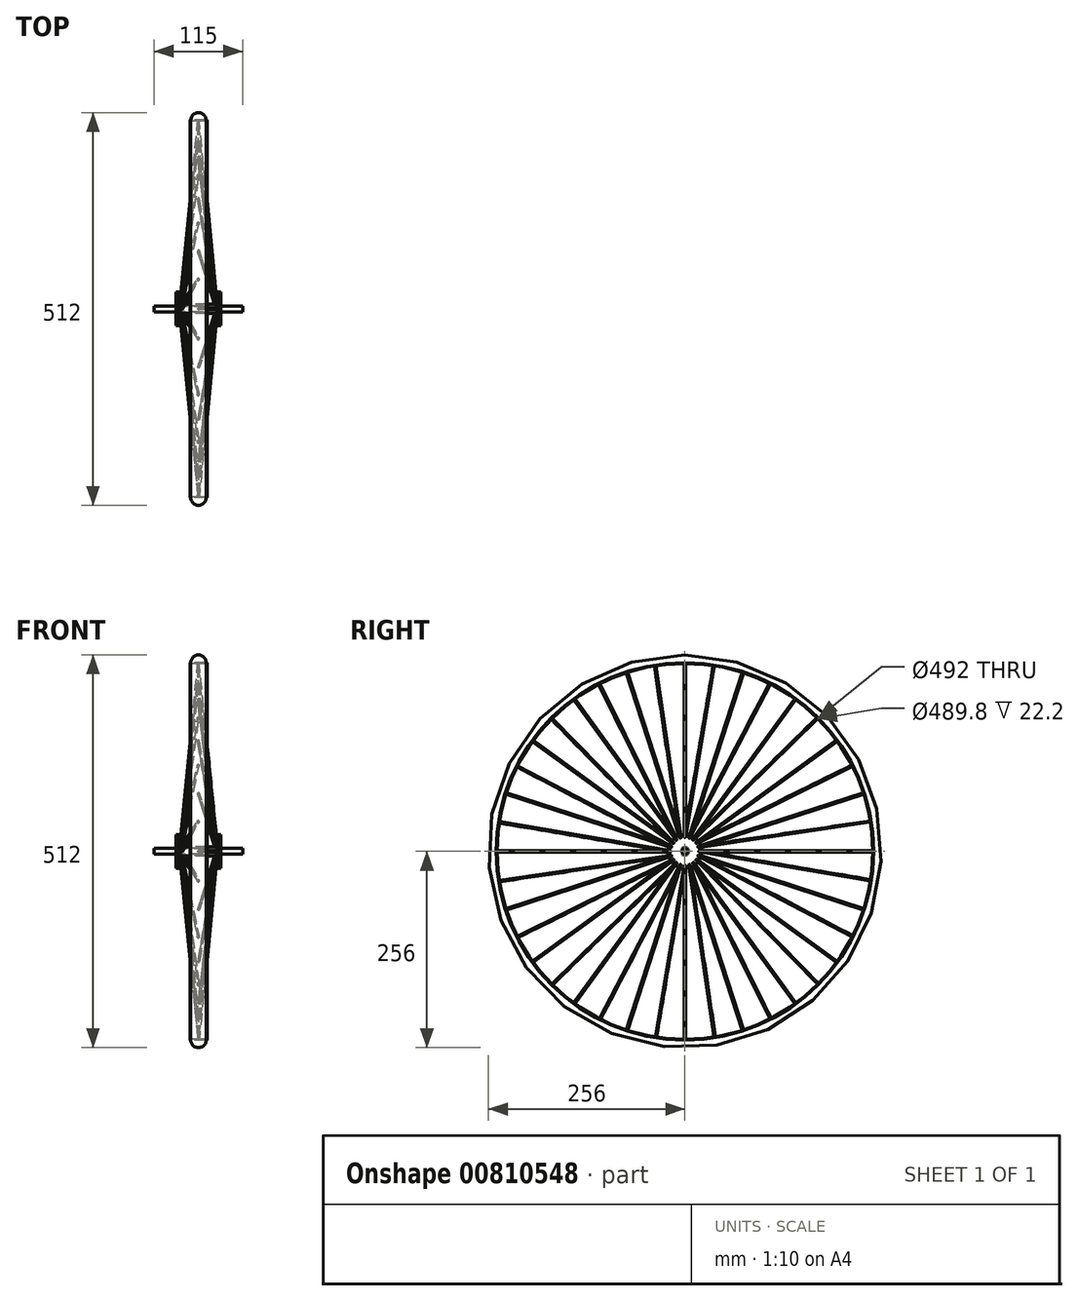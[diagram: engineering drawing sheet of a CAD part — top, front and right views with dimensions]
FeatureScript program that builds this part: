
annotation { "Feature Type Name" : "Feature", "Feature Type Description" : "" }
export const myFeature = defineFeature(function(context is Context, id is Id, definition is map)
    precondition{}
    {
        {
            var Q0;
            Q0=qCreatedBy(makeId("Right.planeOp"),FACE);
            var sketch = newSketch(context, id + "F0", { "sketchPlane" : qUnion([Q0])});
            skCircle(sketch, "E0", {"center": v(0, 0) * mm, "radius": 4 * mm});
            skSolve(sketch);
        }
        {
            var Q0;
            Q0=qCreatedBy(makeId("Front.planeOp"),FACE);
            var sketch = newSketch(context, id + "F1", { "sketchPlane" : qUnion([Q0])});
            skLineSegment(sketch, "E1", {"start": v(0, 6) * mm, "end": v(25, 6) * mm});
            skLineSegment(sketch, "E2", {"start": v(25, 6) * mm, "end": v(25, 22) * mm});
            skLineSegment(sketch, "E3", {"start": v(25, 22) * mm, "end": v(29, 22) * mm});
            skLineSegment(sketch, "E4", {"start": v(29, 22) * mm, "end": v(29, 0) * mm});
            skLineSegment(sketch, "E5", {"start": v(-60.28, 0) * mm, "end": v(66.23, 0) * mm, "construction": true});
            skLineSegment(sketch, "E6.MirrorCS", {"start": v(-29, 22) * mm, "end": v(-29, 0) * mm});
            skLineSegment(sketch, "E7.MirrorCS", {"start": v(-25, 22) * mm, "end": v(-29, 22) * mm});
            skLineSegment(sketch, "E8.MirrorCS", {"start": v(0, 6) * mm, "end": v(-25, 6) * mm});
            skLineSegment(sketch, "E9.MirrorCS", {"start": v(-25, 6) * mm, "end": v(-25, 22) * mm});
            skLineSegment(sketch, "E10", {"start": v(-29, 0) * mm, "end": v(29, 0) * mm});
            skSolve(sketch);
        }
        {
            var Q0;
            Q0 = qSketchRegion(id + "F1", true);
            var Q1;
            Q1=sQuery(id+"F1.wireOp",EDGE,"E5");
            revolve(context, id + "F2", {"surfaceOperationType" : NewSurfaceOperationType.NEW, "entities" : qUnion([Q0]), "axis" : qUnion([Q1]), "revolveType" : RevolveType.FULL});
        }
        {
            var Q0;
            Q0=makeQuery(id+"F2.opRevolve","SWEPT_FACE",FACE,{"disambiguationData":[OSD([sQuery(id+"F1.wireOp",EDGE,"E4")])]});
            var sketch = newSketch(context, id + "F3", { "sketchPlane" : qUnion([Q0])});
            skCircle(sketch, "E11", {"center": v(0, 19) * mm, "radius": 1 * mm});
            skCircle(sketch, "E12.1.0", {"center": v(-5.87, 18.07) * mm, "radius": 1 * mm});
            skCircle(sketch, "E12.2.0", {"center": v(-11.17, 15.37) * mm, "radius": 1 * mm});
            skPoint(sketch, "E12.center", {"position": v(0, 0) * mm});
            skCircle(sketch, "E13.1.3.0", {"center": v(-15.37, 11.17) * mm, "radius": 1 * mm});
            skCircle(sketch, "E13.1.4.0", {"center": v(-18.07, 5.87) * mm, "radius": 1 * mm});
            skCircle(sketch, "E13.1.5.0", {"center": v(-19, 0) * mm, "radius": 1 * mm});
            skCircle(sketch, "E13.1.6.0", {"center": v(-18.07, -5.87) * mm, "radius": 1 * mm});
            skCircle(sketch, "E13.1.7.0", {"center": v(-15.37, -11.17) * mm, "radius": 1 * mm});
            skCircle(sketch, "E13.1.8.0", {"center": v(-11.17, -15.37) * mm, "radius": 1 * mm});
            skCircle(sketch, "E13.1.9.0", {"center": v(-5.87, -18.07) * mm, "radius": 1 * mm});
            skCircle(sketch, "E13.1.10.0", {"center": v(0, -19) * mm, "radius": 1 * mm});
            skCircle(sketch, "E13.1.11.0", {"center": v(5.87, -18.07) * mm, "radius": 1 * mm});
            skCircle(sketch, "E13.1.12.0", {"center": v(11.17, -15.37) * mm, "radius": 1 * mm});
            skCircle(sketch, "E13.1.13.0", {"center": v(15.37, -11.17) * mm, "radius": 1 * mm});
            skCircle(sketch, "E13.1.14.0", {"center": v(18.07, -5.87) * mm, "radius": 1 * mm});
            skCircle(sketch, "E13.1.15.0", {"center": v(19, 0) * mm, "radius": 1 * mm});
            skCircle(sketch, "E13.1.16.0", {"center": v(18.07, 5.87) * mm, "radius": 1 * mm});
            skCircle(sketch, "E13.1.17.0", {"center": v(15.37, 11.17) * mm, "radius": 1 * mm});
            skCircle(sketch, "E13.1.18.0", {"center": v(11.17, 15.37) * mm, "radius": 1 * mm});
            skCircle(sketch, "E13.1.19.0", {"center": v(5.87, 18.07) * mm, "radius": 1 * mm});
            skSolve(sketch);
        }
        {
            var Q0;
            Q0=makeQuery(id+"F3.imprint","IMPRINT",FACE,{"disambiguationData":[TD([[makeQuery(id+"F3.imprint","IMPRINT",EDGE,{"derivedFrom":sQuery(id+"F3.wireOp",EDGE,"E13.1.25.0")}),1.0]])]});
            var Q1;
            Q1=makeQuery(id+"F3.imprint","IMPRINT",FACE,{"disambiguationData":[TD([[makeQuery(id+"F3.imprint","IMPRINT",EDGE,{"derivedFrom":sQuery(id+"F3.wireOp",EDGE,"E13.1.27.0")}),1.0]])]});
            var Q2;
            Q2=makeQuery(id+"F3.imprint","IMPRINT",FACE,{"disambiguationData":[TD([[makeQuery(id+"F3.imprint","IMPRINT",EDGE,{"derivedFrom":sQuery(id+"F3.wireOp",EDGE,"E11")}),1.0]])]});
            var Q3;
            Q3=makeQuery(id+"F3.imprint","IMPRINT",FACE,{"disambiguationData":[TD([[makeQuery(id+"F3.imprint","IMPRINT",EDGE,{"derivedFrom":sQuery(id+"F3.wireOp",EDGE,"E12.1.0")}),1.0]])]});
            var Q4;
            Q4=makeQuery(id+"F3.imprint","IMPRINT",FACE,{"disambiguationData":[TD([[makeQuery(id+"F3.imprint","IMPRINT",EDGE,{"derivedFrom":sQuery(id+"F3.wireOp",EDGE,"E12.2.0")}),1.0]])]});
            var Q5;
            Q5=makeQuery(id+"F3.imprint","IMPRINT",FACE,{"disambiguationData":[TD([[makeQuery(id+"F3.imprint","IMPRINT",EDGE,{"derivedFrom":sQuery(id+"F3.wireOp",EDGE,"E13.1.3.0")}),1.0]])]});
            var Q6;
            Q6=makeQuery(id+"F3.imprint","IMPRINT",FACE,{"disambiguationData":[TD([[makeQuery(id+"F3.imprint","IMPRINT",EDGE,{"derivedFrom":sQuery(id+"F3.wireOp",EDGE,"E13.1.4.0")}),1.0]])]});
            var Q7;
            Q7=makeQuery(id+"F3.imprint","IMPRINT",FACE,{"disambiguationData":[TD([[makeQuery(id+"F3.imprint","IMPRINT",EDGE,{"derivedFrom":sQuery(id+"F3.wireOp",EDGE,"E13.1.5.0")}),1.0]])]});
            var Q8;
            Q8=makeQuery(id+"F3.imprint","IMPRINT",FACE,{"disambiguationData":[TD([[makeQuery(id+"F3.imprint","IMPRINT",EDGE,{"derivedFrom":sQuery(id+"F3.wireOp",EDGE,"E13.1.6.0")}),1.0]])]});
            var Q9;
            Q9=makeQuery(id+"F3.imprint","IMPRINT",FACE,{"disambiguationData":[TD([[makeQuery(id+"F3.imprint","IMPRINT",EDGE,{"derivedFrom":sQuery(id+"F3.wireOp",EDGE,"E13.1.7.0")}),1.0]])]});
            var Q10;
            Q10=makeQuery(id+"F3.imprint","IMPRINT",FACE,{"disambiguationData":[TD([[makeQuery(id+"F3.imprint","IMPRINT",EDGE,{"derivedFrom":sQuery(id+"F3.wireOp",EDGE,"E13.1.8.0")}),1.0]])]});
            var Q11;
            Q11=makeQuery(id+"F3.imprint","IMPRINT",FACE,{"disambiguationData":[TD([[makeQuery(id+"F3.imprint","IMPRINT",EDGE,{"derivedFrom":sQuery(id+"F3.wireOp",EDGE,"E13.1.9.0")}),1.0]])]});
            var Q12;
            Q12=makeQuery(id+"F3.imprint","IMPRINT",FACE,{"disambiguationData":[TD([[makeQuery(id+"F3.imprint","IMPRINT",EDGE,{"derivedFrom":sQuery(id+"F3.wireOp",EDGE,"E13.1.10.0")}),1.0]])]});
            var Q13;
            Q13=makeQuery(id+"F3.imprint","IMPRINT",FACE,{"disambiguationData":[TD([[makeQuery(id+"F3.imprint","IMPRINT",EDGE,{"derivedFrom":sQuery(id+"F3.wireOp",EDGE,"E13.1.11.0")}),1.0]])]});
            var Q14;
            Q14=makeQuery(id+"F3.imprint","IMPRINT",FACE,{"disambiguationData":[TD([[makeQuery(id+"F3.imprint","IMPRINT",EDGE,{"derivedFrom":sQuery(id+"F3.wireOp",EDGE,"E13.1.12.0")}),1.0]])]});
            var Q15;
            Q15=makeQuery(id+"F3.imprint","IMPRINT",FACE,{"disambiguationData":[TD([[makeQuery(id+"F3.imprint","IMPRINT",EDGE,{"derivedFrom":sQuery(id+"F3.wireOp",EDGE,"E13.1.13.0")}),1.0]])]});
            var Q16;
            Q16=makeQuery(id+"F3.imprint","IMPRINT",FACE,{"disambiguationData":[TD([[makeQuery(id+"F3.imprint","IMPRINT",EDGE,{"derivedFrom":sQuery(id+"F3.wireOp",EDGE,"E13.1.14.0")}),1.0]])]});
            var Q17;
            Q17=makeQuery(id+"F3.imprint","IMPRINT",FACE,{"disambiguationData":[TD([[makeQuery(id+"F3.imprint","IMPRINT",EDGE,{"derivedFrom":sQuery(id+"F3.wireOp",EDGE,"E13.1.15.0")}),1.0]])]});
            var Q18;
            Q18=makeQuery(id+"F3.imprint","IMPRINT",FACE,{"disambiguationData":[TD([[makeQuery(id+"F3.imprint","IMPRINT",EDGE,{"derivedFrom":sQuery(id+"F3.wireOp",EDGE,"E13.1.18.0")}),1.0]])]});
            var Q19;
            Q19=makeQuery(id+"F3.imprint","IMPRINT",FACE,{"disambiguationData":[TD([[makeQuery(id+"F3.imprint","IMPRINT",EDGE,{"derivedFrom":sQuery(id+"F3.wireOp",EDGE,"E13.1.17.0")}),1.0]])]});
            var Q20;
            Q20=makeQuery(id+"F3.imprint","IMPRINT",FACE,{"disambiguationData":[TD([[makeQuery(id+"F3.imprint","IMPRINT",EDGE,{"derivedFrom":sQuery(id+"F3.wireOp",EDGE,"E13.1.16.0")}),1.0]])]});
            var Q21;
            Q21=makeQuery(id+"F3.imprint","IMPRINT",FACE,{"disambiguationData":[TD([[makeQuery(id+"F3.imprint","IMPRINT",EDGE,{"derivedFrom":sQuery(id+"F3.wireOp",EDGE,"E13.1.19.0")}),1.0]])]});
            var Q22;
            Q22=makeQuery(id+"F3.imprint","IMPRINT",FACE,{"disambiguationData":[TD([[makeQuery(id+"F3.imprint","IMPRINT",EDGE,{"derivedFrom":sQuery(id+"F3.wireOp",EDGE,"E13.1.20.0")}),1.0]])]});
            var Q23;
            Q23=makeQuery(id+"F3.imprint","IMPRINT",FACE,{"disambiguationData":[TD([[makeQuery(id+"F3.imprint","IMPRINT",EDGE,{"derivedFrom":sQuery(id+"F3.wireOp",EDGE,"E13.1.21.0")}),1.0]])]});
            var Q24;
            Q24=makeQuery(id+"F3.imprint","IMPRINT",FACE,{"disambiguationData":[TD([[makeQuery(id+"F3.imprint","IMPRINT",EDGE,{"derivedFrom":sQuery(id+"F3.wireOp",EDGE,"E13.1.22.0")}),1.0]])]});
            var Q25;
            Q25=makeQuery(id+"F3.imprint","IMPRINT",FACE,{"disambiguationData":[TD([[makeQuery(id+"F3.imprint","IMPRINT",EDGE,{"derivedFrom":sQuery(id+"F3.wireOp",EDGE,"E13.1.24.0")}),1.0]])]});
            var Q26;
            Q26=makeQuery(id+"F3.imprint","IMPRINT",FACE,{"disambiguationData":[TD([[makeQuery(id+"F3.imprint","IMPRINT",EDGE,{"derivedFrom":sQuery(id+"F3.wireOp",EDGE,"E13.1.26.0")}),1.0]])]});
            var Q27;
            Q27=makeQuery(id+"F3.imprint","IMPRINT",FACE,{"disambiguationData":[TD([[makeQuery(id+"F3.imprint","IMPRINT",EDGE,{"derivedFrom":sQuery(id+"F3.wireOp",EDGE,"E13.1.23.0")}),1.0]])]});
            extrude(context, id + "F4", {"entities" : qUnion([Q0, Q1, Q2, Q3, Q4, Q5, Q6, Q7, Q8, Q9, Q10, Q11, Q12, Q13, Q14, Q15, Q16, Q17, Q18, Q19, Q20, Q21, Q22, Q23, Q24, Q25, Q26, Q27]), "operationType" : NewBodyOperationType.REMOVE, "endBound" : BoundingType.THROUGH_ALL, "oppositeDirection" : true, "depth" : 25 * mm, "offsetDistance" : 25 * mm});
        }
        {
            var Q0;
            Q0=qCreatedBy(makeId("Front.planeOp"),FACE);
            var sketch = newSketch(context, id + "F5", { "sketchPlane" : qUnion([Q0])});
            skLineSegment(sketch, "E14", {"start": v(0, 0) * mm, "end": v(0, 256) * mm, "construction": true});
            skArc(sketch, "E15", {"start": v(10, 246) * mm, "mid": v(0, 256) * mm, "end": v(-10, 246) * mm});
            skLineSegment(sketch, "E16", {"start": v(-10, 246) * mm, "end": v(10, 246) * mm});
            skSolve(sketch);
        }
        {
            var Q0;
            Q0 = qSketchRegion(id + "F5", true);
            var Q1;
            Q1=sQuery(id+"F1.wireOp",EDGE,"E5");
            revolve(context, id + "F6", {"surfaceOperationType" : NewSurfaceOperationType.NEW, "entities" : qUnion([Q0]), "axis" : qUnion([Q1]), "revolveType" : RevolveType.FULL});
        }
        {
            var Q0;
            Q0=qCreatedBy(makeId("Front.planeOp"),FACE);
            var sketch = newSketch(context, id + "F7", { "sketchPlane" : qUnion([Q0])});
            skLineSegment(sketch, "E17", {"start": v(10.1, 245.9) * mm, "end": v(0, 245.9) * mm});
            skLineSegment(sketch, "E18", {"start": v(10.1, 245.9) * mm, "end": v(10.1, 246.1) * mm});
            skLineSegment(sketch, "E19.0", {"start": v(11.1, 244.9) * mm, "end": v(11.1, 246.1) * mm});
            skLineSegment(sketch, "E20.0", {"start": v(11.1, 244.9) * mm, "end": v(0, 244.9) * mm});
            skLineSegment(sketch, "E21.0", {"start": v(10.1, 244.9) * mm, "end": v(0, 244.9) * mm});
            skLineSegment(sketch, "E22", {"start": v(10.1, 246.1) * mm, "end": v(11.1, 246.1) * mm});
            skLineSegment(sketch, "E23.MirrorCS", {"start": v(-10.1, 245.9) * mm, "end": v(0, 245.9) * mm});
            skLineSegment(sketch, "E24.MirrorCS", {"start": v(-10.1, 246.1) * mm, "end": v(-11.1, 246.1) * mm});
            skLineSegment(sketch, "E25.MirrorCS", {"start": v(-11.1, 244.9) * mm, "end": v(0, 244.9) * mm});
            skLineSegment(sketch, "E26.MirrorCS", {"start": v(-11.1, 244.9) * mm, "end": v(-11.1, 246.1) * mm});
            skLineSegment(sketch, "E27.MirrorCS", {"start": v(-10.1, 245.9) * mm, "end": v(-10.1, 246.1) * mm});
            skSolve(sketch);
        }
        {
            var Q0;
            Q0=makeQuery(id+"F7.imprint","IMPRINT",FACE,{"disambiguationData":[TD([[makeQuery(id+"F7.imprint","IMPRINT",EDGE,{"derivedFrom":sQuery(id+"F7.wireOp",EDGE,"E17")}),1.0]])]});
            var Q1;
            Q1=sQuery(id+"F1.wireOp",EDGE,"E5");
            revolve(context, id + "F8", {"surfaceOperationType" : NewSurfaceOperationType.NEW, "entities" : qUnion([Q0]), "axis" : qUnion([Q1]), "revolveType" : RevolveType.FULL});
        }
        {
            var Q0;
            Q0=qCreatedBy(makeId("Top.planeOp"),FACE);
            var Q1;
            Q1=sQuery(id+"F7.wireOp",EDGE,"E21.0");
            cPlane(context, id + "F9", {"entities" : qUnion([Q0, Q1]), "cplaneType" : CPlaneType.LINE_ANGLE, "offset" : 25 * mm, "angle" : 180 * degree, "width" : 150 * mm, "height" : 150 * mm});
        }
        {
            var Q0;
            Q0=qCreatedBy(id+"F9.planeOp",FACE);
            var sketch = newSketch(context, id + "F10", { "sketchPlane" : qUnion([Q0])});
            skPoint(sketch, "E28", {"position": v(0, 0) * mm});
            skCircle(sketch, "E29", {"center": v(0, 0) * mm, "radius": 2.62 * mm});
            skSolve(sketch);
        }
        {
            var Q0;
            Q0=qCreatedBy(makeId("Front.planeOp"),FACE);
            var sketch = newSketch(context, id + "F11", { "sketchPlane" : qUnion([Q0])});
            skLineSegment(sketch, "E30", {"start": v(0, 244.9) * mm, "end": v(22.01, 21.7) * mm});
            skLineSegment(sketch, "E31", {"start": v(25, 19) * mm, "end": v(29, 19) * mm});
            skPoint(sketch, "E32.visualSharp", {"position": v(22.28, 19) * mm});
            skArc(sketch, "E32.filletArc", {"start": v(22.01, 21.7) * mm, "mid": v(22.99, 19.78) * mm, "end": v(25, 19) * mm});
            skSolve(sketch);
        }
        {
            var Q0;
            Q0=sQuery(id+"F10.wireOp",VERTEX,"E28");
            var Q1;
            Q1=qCreatedBy(makeId("Right.planeOp"),FACE);
            cPlane(context, id + "F12", {"entities" : qUnion([Q0, Q1]), "cplaneType" : CPlaneType.PLANE_POINT, "offset" : 25 * mm, "width" : 150 * mm, "height" : 150 * mm});
        }
        {
            var Q0;
            Q0=qCreatedBy(id+"F12.planeOp",FACE);
            var sketch = newSketch(context, id + "F13", { "sketchPlane" : qUnion([Q0])});
            skPoint(sketch, "E33.0", {"position": v(0, 244.9) * mm});
            skPoint(sketch, "E34.1.0", {"position": v(-38.31, 241.9) * mm});
            skPoint(sketch, "E34.2.0", {"position": v(-75.68, 232.92) * mm});
            skPoint(sketch, "E34.3.0", {"position": v(-111.19, 218.21) * mm});
            skPoint(sketch, "E34.4.0", {"position": v(-143.95, 198.13) * mm});
            skPoint(sketch, "E34.5.0", {"position": v(-173.18, 173.18) * mm});
            skPoint(sketch, "E34.6.0", {"position": v(-198.13, 143.95) * mm});
            skPoint(sketch, "E34.7.0", {"position": v(-218.21, 111.19) * mm});
            skPoint(sketch, "E34.8.0", {"position": v(-232.92, 75.68) * mm});
            skPoint(sketch, "E34.9.0", {"position": v(-241.9, 38.31) * mm});
            skPoint(sketch, "E34.10.0", {"position": v(-244.9, 0) * mm});
            skPoint(sketch, "E34.11.0", {"position": v(-241.9, -38.31) * mm});
            skPoint(sketch, "E34.12.0", {"position": v(-232.92, -75.68) * mm});
            skPoint(sketch, "E34.13.0", {"position": v(-218.21, -111.19) * mm});
            skPoint(sketch, "E34.14.0", {"position": v(-198.13, -143.95) * mm});
            skPoint(sketch, "E34.15.0", {"position": v(-173.18, -173.18) * mm});
            skPoint(sketch, "E34.16.0", {"position": v(-143.95, -198.13) * mm});
            skPoint(sketch, "E34.17.0", {"position": v(-111.19, -218.21) * mm});
            skPoint(sketch, "E34.18.0", {"position": v(-75.68, -232.92) * mm});
            skPoint(sketch, "E34.19.0", {"position": v(-38.31, -241.9) * mm});
            skPoint(sketch, "E34.20.0", {"position": v(0, -244.9) * mm});
            skPoint(sketch, "E34.21.0", {"position": v(38.31, -241.9) * mm});
            skPoint(sketch, "E34.22.0", {"position": v(75.68, -232.92) * mm});
            skPoint(sketch, "E34.23.0", {"position": v(111.19, -218.21) * mm});
            skPoint(sketch, "E34.24.0", {"position": v(143.95, -198.13) * mm});
            skPoint(sketch, "E34.25.0", {"position": v(173.18, -173.18) * mm});
            skPoint(sketch, "E34.26.0", {"position": v(198.13, -143.95) * mm});
            skPoint(sketch, "E34.27.0", {"position": v(218.21, -111.19) * mm});
            skPoint(sketch, "E34.28.0", {"position": v(232.92, -75.68) * mm});
            skPoint(sketch, "E34.29.0", {"position": v(241.9, -38.31) * mm});
            skPoint(sketch, "E34.30.0", {"position": v(244.9, 0) * mm});
            skPoint(sketch, "E34.31.0", {"position": v(241.9, 38.31) * mm});
            skPoint(sketch, "E34.32.0", {"position": v(232.92, 75.68) * mm});
            skPoint(sketch, "E34.33.0", {"position": v(218.21, 111.19) * mm});
            skPoint(sketch, "E34.34.0", {"position": v(198.13, 143.95) * mm});
            skPoint(sketch, "E34.35.0", {"position": v(173.18, 173.18) * mm});
            skPoint(sketch, "E34.36.0", {"position": v(143.95, 198.13) * mm});
            skPoint(sketch, "E34.37.0", {"position": v(111.19, 218.21) * mm});
            skPoint(sketch, "E34.38.0", {"position": v(75.68, 232.92) * mm});
            skPoint(sketch, "E34.39.0", {"position": v(38.31, 241.9) * mm});
            skPoint(sketch, "E34.center", {"position": v(0, 0) * mm});
            skSolve(sketch);
        }
        {
            var Q0;
            Q0=sQuery(id+"F13.wireOp",VERTEX,"E34.1.0");
            var Q1;
            Q1=sQuery(id+"F1.wireOp",VERTEX,"E5.end");
            var Q2;
            Q2=sQuery(id+"F1.wireOp",VERTEX,"E5.start");
            cPlane(context, id + "F14", {"entities" : qUnion([Q0, Q1, Q2]), "cplaneType" : CPlaneType.THREE_POINT, "offset" : 25 * mm, "width" : 150 * mm, "height" : 150 * mm});
        }
        {
            var Q0;
            Q0=sQuery(id+"F3.wireOp",VERTEX,"E11.center");
            var Q1;
            Q1=sQuery(id+"F11.wireOp",EDGE,"E31");
            cPlane(context, id + "F15", {"entities" : qUnion([Q0, Q1]), "cplaneType" : CPlaneType.LINE_POINT, "offset" : 25 * mm, "width" : 150 * mm, "height" : 150 * mm});
        }
        {
            var Q0;
            Q0=qCreatedBy(id+"F15.planeOp",FACE);
            var sketch = newSketch(context, id + "F16", { "sketchPlane" : qUnion([Q0])});
            skCircle(sketch, "E35", {"center": v(0, 19) * mm, "radius": 0.99 * mm});
            skSolve(sketch);
        }
        {
            var Q0;
            Q0 = qSketchRegion(id + "F16", true);
            var Q1;
            Q1=sQuery(id+"F11.wireOp",EDGE,"E31");
            var Q2;
            Q2=sQuery(id+"F11.wireOp",EDGE,"E32.filletArc");
            var Q3;
            Q3=sQuery(id+"F11.wireOp",EDGE,"E30");
            sweep(context, id + "F17", {"profiles" : qUnion([Q0]), "path" : qUnion([Q1, Q2, Q3])});
        }
        {
            var Q0;
            Q0=makeQuery(id+"F17.opSweep","SWEPT_BODY",BODY,{"disambiguationData":[OSD([sQuery(id+"F11.wireOp",EDGE,"E30"),sQuery(id+"F16.wireOp",EDGE,"E35")])]});
            var Q1;
            Q1=sQuery(id+"F1.wireOp",EDGE,"E5");
            circularPattern(context, id + "F18", {"operationType" : NewBodyOperationType.ADD, "entities" : qUnion([Q0]), "axis" : qUnion([Q1]), "angle" : 360 * degree, "instanceCount" : 20, "equalSpace" : true});
        }
        {
            var Q0;
            Q0=sQuery(id+"F1.wireOp",VERTEX,"E5.start");
            var Q1;
            Q1=sQuery(id+"F1.wireOp",EDGE,"E5");
            cPlane(context, id + "F19", {"entities" : qUnion([Q0, Q1]), "cplaneType" : CPlaneType.LINE_POINT, "offset" : 25 * mm, "width" : 150 * mm, "height" : 150 * mm});
        }
        {
            var Q0;
            Q0=qCreatedBy(id+"F19.planeOp",FACE);
            var sketch = newSketch(context, id + "F20", { "sketchPlane" : qUnion([Q0])});
            skLineSegment(sketch, "E36", {"start": v(0, 0) * mm, "end": v(0, 277.89) * mm, "construction": true});
            skLineSegment(sketch, "E37", {"start": v(0, 0) * mm, "end": v(-46.65, 294.55) * mm, "construction": true});
            skSolve(sketch);
        }
        {
            var Q0;
            Q0=makeQuery(id+"F2.opRevolve","SWEPT_FACE",FACE,{"disambiguationData":[OSD([sQuery(id+"F1.wireOp",EDGE,"E6.MirrorCS")])]});
            var sketch = newSketch(context, id + "F21", { "sketchPlane" : qUnion([Q0])});
            skPoint(sketch, "E38", {"position": v(5.87, 18.07) * mm});
            skCircle(sketch, "E39", {"center": v(5.87, 18.07) * mm, "radius": 0.9 * mm});
            skSolve(sketch);
        }
        {
            var Q0;
            Q0=makeQuery(id+"F2.opRevolve","SWEPT_FACE",FACE,{"disambiguationData":[OSD([sQuery(id+"F1.wireOp",EDGE,"E9.MirrorCS")])]});
            var sketch = newSketch(context, id + "F22", { "sketchPlane" : qUnion([Q0])});
            skPoint(sketch, "E40", {"position": v(-5.87, 18.07) * mm});
            skSolve(sketch);
        }
        {
            var Q0;
            Q0=sQuery(id+"F21.wireOp",VERTEX,"E38");
            var Q1;
            Q1=sQuery(id+"F20.wireOp",VERTEX,"E37.end");
            var Q2;
            Q2=sQuery(id+"F22.wireOp",VERTEX,"E40");
            cPlane(context, id + "F23", {"entities" : qUnion([Q0, Q1, Q2]), "cplaneType" : CPlaneType.THREE_POINT, "offset" : 25 * mm, "width" : 150 * mm, "height" : 150 * mm});
        }
        {
            var Q0;
            Q0=qCreatedBy(id+"F23.planeOp",FACE);
            var sketch = newSketch(context, id + "F24", { "sketchPlane" : qUnion([Q0])});
            skLineSegment(sketch, "E41", {"start": v(-29, 18.73) * mm, "end": v(-25, 18.73) * mm});
            skLineSegment(sketch, "E42", {"start": v(-22.01, 21.44) * mm, "end": v(0, 247.71) * mm});
            skPoint(sketch, "E43.visualSharp", {"position": v(-22.28, 18.73) * mm});
            skArc(sketch, "E43.filletArc", {"start": v(-25, 18.73) * mm, "mid": v(-22.98, 19.51) * mm, "end": v(-22.01, 21.44) * mm});
            skSolve(sketch);
        }
        {
            var Q0;
            Q0=makeQuery(id+"F21.imprint","IMPRINT",FACE,{"disambiguationData":[TD([[makeQuery(id+"F21.imprint","IMPRINT",EDGE,{"derivedFrom":sQuery(id+"F21.wireOp",EDGE,"E39")}),1.0]])]});
            var Q1;
            Q1=sQuery(id+"F24.wireOp",EDGE,"E41");
            var Q2;
            Q2=sQuery(id+"F24.wireOp",EDGE,"E43.filletArc");
            var Q3;
            Q3=sQuery(id+"F24.wireOp",EDGE,"E42");
            sweep(context, id + "F25", {"profiles" : qUnion([Q0]), "path" : qUnion([Q1, Q2, Q3])});
        }
        {
            var Q0;
            Q0=makeQuery(id+"F25.opSweep","SWEPT_BODY",BODY,{"disambiguationData":[OSD([sQuery(id+"F21.wireOp",EDGE,"E39"),sQuery(id+"F24.wireOp",EDGE,"E42")])]});
            var Q1;
            Q1=sQuery(id+"F1.wireOp",EDGE,"E5");
            circularPattern(context, id + "F26", {"operationType" : NewBodyOperationType.ADD, "entities" : qUnion([Q0]), "axis" : qUnion([Q1]), "angle" : 360 * degree, "instanceCount" : 20, "equalSpace" : true});
        }
        {
            var Q0;
            Q0=makeQuery(id+"F2.opRevolve","SWEPT_FACE",FACE,{"disambiguationData":[OSD([sQuery(id+"F1.wireOp",EDGE,"E4")])]});
            var sketch = newSketch(context, id + "F27", { "sketchPlane" : qUnion([Q0])});
            skCircle(sketch, "E44.0", {"center": v(0, 0) * mm, "radius": 4 * mm});
            skSolve(sketch);
        }
        {
            var Q0;
            Q0=makeQuery(id+"F27.imprint","IMPRINT",FACE,{"disambiguationData":[TD([[makeQuery(id+"F27.imprint","IMPRINT",EDGE,{"derivedFrom":sQuery(id+"F27.wireOp",EDGE,"E44.0")}),1.0]])]});
            extrude(context, id + "F28", {"entities" : qUnion([Q0]), "operationType" : NewBodyOperationType.REMOVE, "endBound" : BoundingType.THROUGH_ALL, "oppositeDirection" : true, "depth" : 25 * mm, "offsetDistance" : 25 * mm});
        }
        {
            var Q0;
            Q0=qCreatedBy(makeId("Right.planeOp"),FACE);
            var sketch = newSketch(context, id + "F29", { "sketchPlane" : qUnion([Q0])});
            skCircle(sketch, "E45", {"center": v(0, 0) * mm, "radius": 3.9 * mm});
            skSolve(sketch);
        }
        {
            var Q0;
            Q0 = qSketchRegion(id + "F29", true);
            extrude(context, id + "F30", {"entities" : qUnion([Q0]), "endBound" : BoundingType.SYMMETRIC, "depth" : 115 * mm, "offsetDistance" : 25 * mm});
        }
    });
